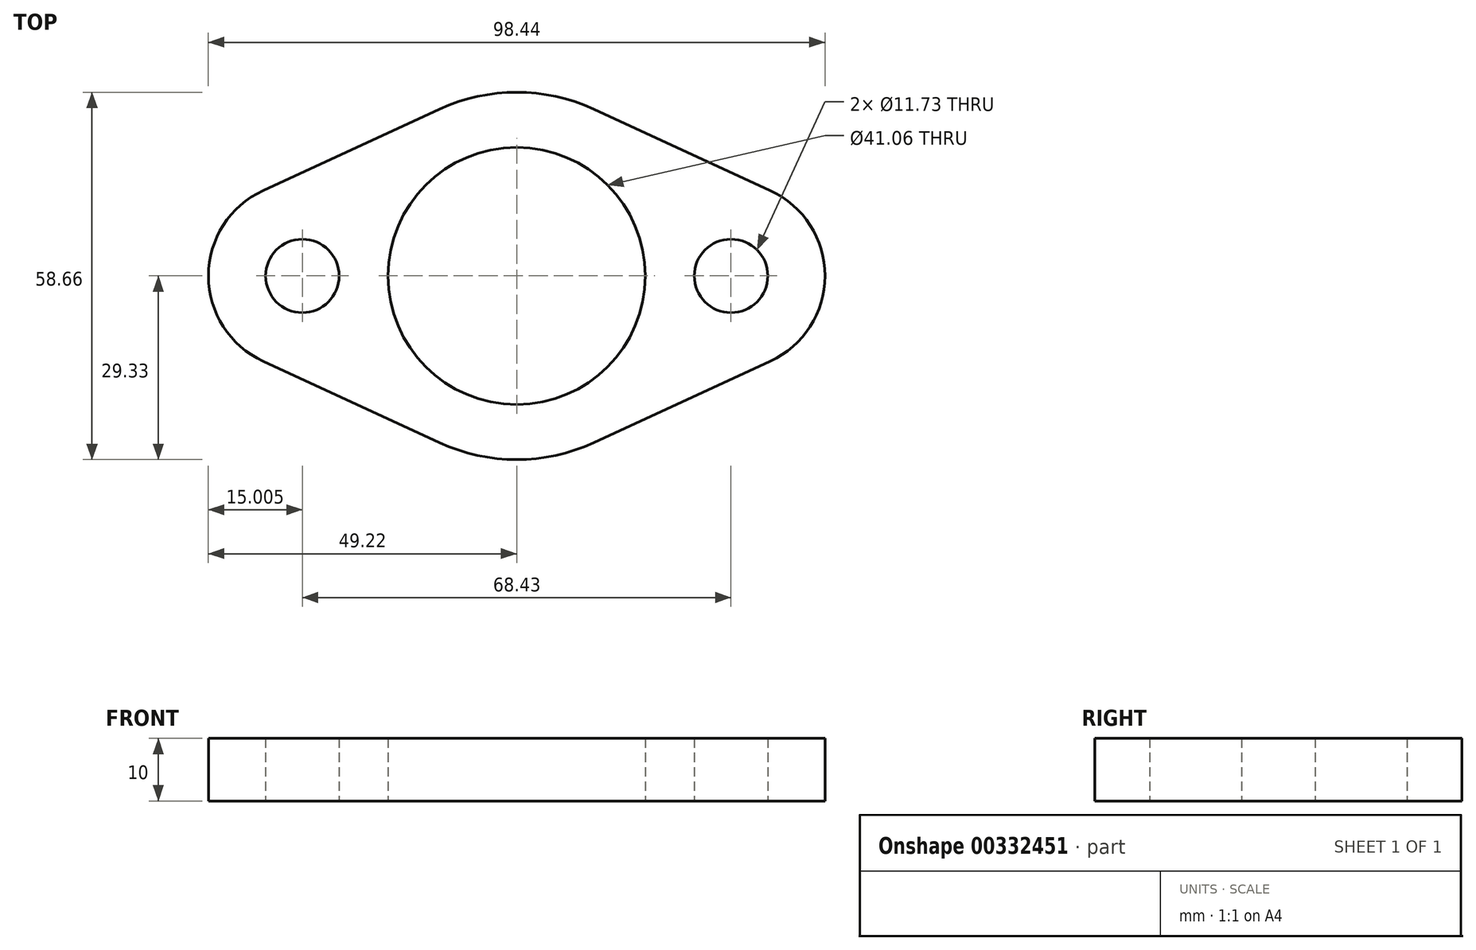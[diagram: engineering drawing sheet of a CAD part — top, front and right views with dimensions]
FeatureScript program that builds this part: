
annotation { "Feature Type Name" : "Feature", "Feature Type Description" : "" }
export const myFeature = defineFeature(function(context is Context, id is Id, definition is map)
    precondition{}
    {
        {
            var Q0;
            Q0=qCreatedBy(makeId("Top.planeOp"),FACE);
            var sketch = newSketch(context, id + "F0", { "sketchPlane" : qUnion([Q0])});
            skCircle(sketch, "E0", {"center": v(0, 0) * mm, "radius": 20.53 * mm});
            skArc(sketch, "E1", {"start": v(-12.28, -26.63) * mm, "mid": v(0, -29.33) * mm, "end": v(12.28, -26.63) * mm});
            skCircle(sketch, "E2", {"center": v(34.22, 0) * mm, "radius": 5.87 * mm});
            skCircle(sketch, "E3", {"center": v(-34.22, 0) * mm, "radius": 5.87 * mm});
            skArc(sketch, "E4", {"start": v(40.5, -13.62) * mm, "mid": v(49.22, 0) * mm, "end": v(40.5, 13.62) * mm});
            skArc(sketch, "E5", {"start": v(-40.5, 13.62) * mm, "mid": v(-49.22, 0) * mm, "end": v(-40.5, -13.62) * mm});
            skLineSegment(sketch, "E6", {"start": v(-40.5, 13.62) * mm, "end": v(-12.28, 26.63) * mm});
            skLineSegment(sketch, "E7", {"start": v(12.28, 26.63) * mm, "end": v(40.5, 13.62) * mm});
            skLineSegment(sketch, "E8", {"start": v(-40.5, -13.62) * mm, "end": v(-12.28, -26.63) * mm});
            skLineSegment(sketch, "E9", {"start": v(12.28, -26.63) * mm, "end": v(40.5, -13.62) * mm});
            skArc(sketch, "E10.trimOffspring", {"start": v(12.28, 26.63) * mm, "mid": v(0, 29.33) * mm, "end": v(-12.28, 26.63) * mm});
            skSolve(sketch);
        }
        {
            var Q0;
            Q0 = qSketchRegion(id + "F0", true);
            extrude(context, id + "F1", {"entities" : qUnion([Q0]), "depth" : 10 * mm});
        }
    });
